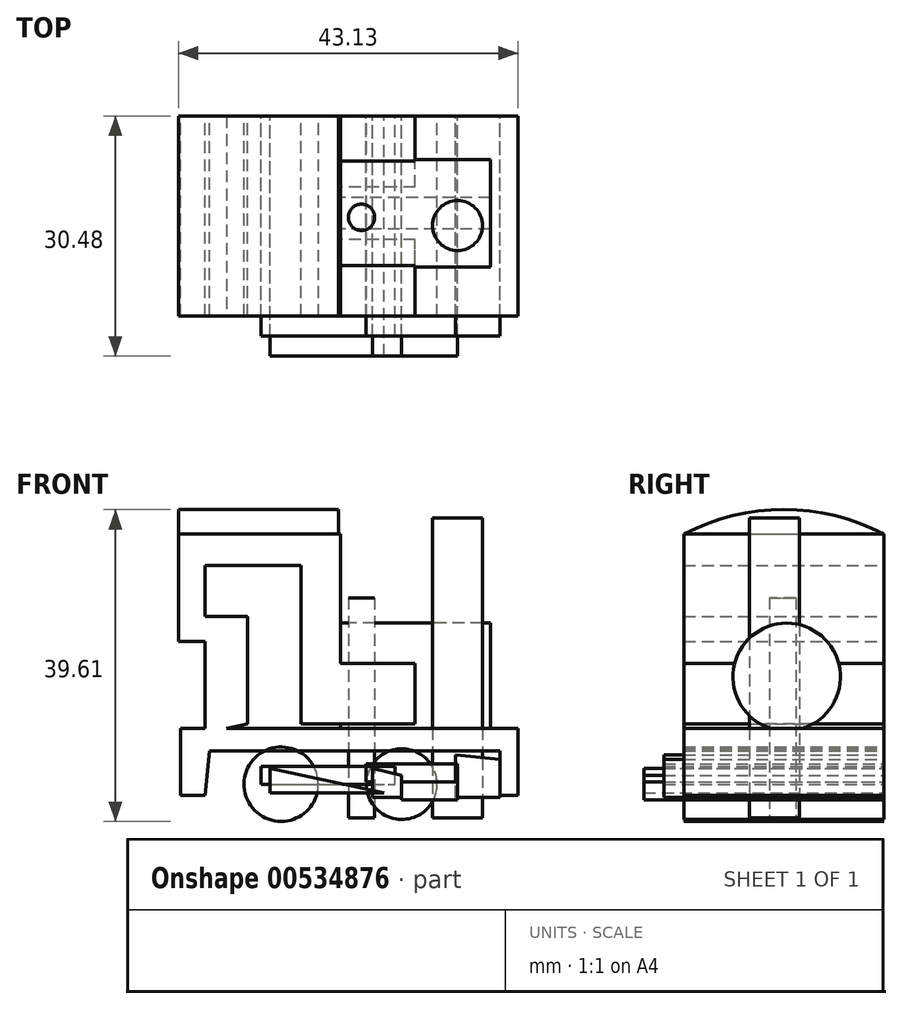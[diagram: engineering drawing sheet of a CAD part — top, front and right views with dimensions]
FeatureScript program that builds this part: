
annotation { "Feature Type Name" : "Feature", "Feature Type Description" : "" }
export const myFeature = defineFeature(function(context is Context, id is Id, definition is map)
    precondition{}
    {
        {
            var Q0;
            Q0=qCreatedBy(makeId("Front.planeOp"),FACE);
            var sketch = newSketch(context, id + "F0", { "sketchPlane" : qUnion([Q0])});
            skCircle(sketch, "E0", {"center": v(7.8, 4.26) * mm, "radius": 4.49 * mm});
            skCircle(sketch, "E1", {"center": v(-7.52, 4.26) * mm, "radius": 4.72 * mm});
            skSolve(sketch);
        }
        {
            var Q0;
            Q0=makeQuery(id+"F0.imprint","IMPRINT",FACE,{"disambiguationData":[TD([[makeQuery(id+"F0.imprint","IMPRINT",EDGE,{"derivedFrom":sQuery(id+"F0.wireOp",EDGE,"E0")}),1.0]])]});
            var Q1;
            Q1=makeQuery(id+"F0.imprint","IMPRINT",FACE,{"disambiguationData":[TD([[makeQuery(id+"F0.imprint","IMPRINT",EDGE,{"derivedFrom":sQuery(id+"F0.wireOp",EDGE,"E1")}),1.0]])]});
            extrude(context, id + "F1", {"entities" : qUnion([Q0, Q1]), "depth" : 25.4 * mm, "offsetDistance" : 25.4 * mm});
        }
        {
            var Q0;
            Q0=qCreatedBy(makeId("Front.planeOp"),FACE);
            var sketch = newSketch(context, id + "F2", { "sketchPlane" : qUnion([Q0])});
            skLineSegment(sketch, "E2", {"start": v(-16.6, 8.51) * mm, "end": v(20.29, 8.51) * mm});
            skLineSegment(sketch, "E3", {"start": v(20.29, 8.51) * mm, "end": v(20.29, 2.84) * mm});
            skLineSegment(sketch, "E4", {"start": v(20.29, 2.84) * mm, "end": v(22.56, 2.84) * mm});
            skLineSegment(sketch, "E5", {"start": v(22.56, 2.84) * mm, "end": v(22.56, 11.35) * mm});
            skLineSegment(sketch, "E6", {"start": v(22.56, 11.35) * mm, "end": v(-20.29, 11.35) * mm});
            skLineSegment(sketch, "E7", {"start": v(-20.29, 11.35) * mm, "end": v(-20.29, 2.84) * mm});
            skLineSegment(sketch, "E8", {"start": v(-20.29, 2.84) * mm, "end": v(-17.17, 2.84) * mm});
            skLineSegment(sketch, "E9", {"start": v(-17.17, 2.84) * mm, "end": v(-16.6, 8.51) * mm});
            skSolve(sketch);
        }
        {
            var Q0;
            Q0=makeQuery(id+"F2.imprint","IMPRINT",FACE,{"disambiguationData":[TD([[makeQuery(id+"F2.imprint","IMPRINT",EDGE,{"derivedFrom":sQuery(id+"F2.wireOp",EDGE,"E2")}),1.0]])]});
            extrude(context, id + "F3", {"entities" : qUnion([Q0]), "depth" : 25.4 * mm, "offsetDistance" : 25.4 * mm});
        }
        {
            var Q0;
            Q0=qCreatedBy(makeId("Front.planeOp"),FACE);
            var sketch = newSketch(context, id + "F4", { "sketchPlane" : qUnion([Q0])});
            skLineSegment(sketch, "E10", {"start": v(-17.17, 10.78) * mm, "end": v(-17.17, 22.41) * mm});
            skLineSegment(sketch, "E11", {"start": v(-17.17, 22.41) * mm, "end": v(-20.57, 22.41) * mm});
            skLineSegment(sketch, "E12", {"start": v(-20.57, 22.41) * mm, "end": v(-20.57, 36.03) * mm});
            skLineSegment(sketch, "E13", {"start": v(-20.57, 36.03) * mm, "end": v(0, 36.03) * mm});
            skLineSegment(sketch, "E14", {"start": v(0, 36.03) * mm, "end": v(0, 19.58) * mm});
            skLineSegment(sketch, "E15", {"start": v(0, 19.58) * mm, "end": v(9.5, 19.58) * mm});
            skLineSegment(sketch, "E16", {"start": v(9.5, 19.58) * mm, "end": v(9.5, 11.92) * mm});
            skLineSegment(sketch, "E17", {"start": v(9.5, 11.92) * mm, "end": v(-4.97, 11.92) * mm});
            skLineSegment(sketch, "E18", {"start": v(-4.97, 11.92) * mm, "end": v(-4.97, 32.06) * mm});
            skLineSegment(sketch, "E19", {"start": v(-4.97, 32.06) * mm, "end": v(-17.17, 32.06) * mm});
            skLineSegment(sketch, "E20", {"start": v(-17.17, 32.06) * mm, "end": v(-17.17, 25.54) * mm});
            skLineSegment(sketch, "E21", {"start": v(-17.17, 25.54) * mm, "end": v(-11.77, 25.54) * mm});
            skLineSegment(sketch, "E22", {"start": v(-11.77, 25.54) * mm, "end": v(-11.77, 11.92) * mm});
            skLineSegment(sketch, "E23", {"start": v(-11.77, 11.92) * mm, "end": v(-17.17, 10.78) * mm});
            skSolve(sketch);
        }
        {
            var Q0;
            Q0=makeQuery(id+"F4.imprint","IMPRINT",FACE,{"disambiguationData":[TD([[makeQuery(id+"F4.imprint","IMPRINT",EDGE,{"derivedFrom":sQuery(id+"F4.wireOp",EDGE,"E10")}),-1.0]])]});
            extrude(context, id + "F5", {"entities" : qUnion([Q0]), "operationType" : NewBodyOperationType.ADD, "depth" : 25.4 * mm, "offsetDistance" : 25.4 * mm});
        }
        {
            var Q0;
            Q0=qCreatedBy(makeId("Right.planeOp"),FACE);
            var sketch = newSketch(context, id + "F6", { "sketchPlane" : qUnion([Q0])});
            skCircle(sketch, "E24", {"center": v(-12.34, 17.87) * mm, "radius": 6.83 * mm});
            skSolve(sketch);
        }
        {
            var Q0;
            Q0=makeQuery(id+"F6.imprint","IMPRINT",FACE,{"disambiguationData":[TD([[makeQuery(id+"F6.imprint","IMPRINT",EDGE,{"derivedFrom":sQuery(id+"F6.wireOp",EDGE,"E24")}),1.0]])]});
            extrude(context, id + "F7", {"entities" : qUnion([Q0]), "operationType" : NewBodyOperationType.ADD, "depth" : 19.05 * mm, "offsetDistance" : 25.4 * mm});
        }
        {
            var Q0;
            Q0=qCreatedBy(makeId("Top.planeOp"),FACE);
            var sketch = newSketch(context, id + "F8", { "sketchPlane" : qUnion([Q0])});
            skCircle(sketch, "E25", {"center": v(14.9, -13.9) * mm, "radius": 3.17 * mm});
            skSolve(sketch);
        }
        {
            var Q0;
            Q0=makeQuery(id+"F8.imprint","IMPRINT",FACE,{"disambiguationData":[TD([[makeQuery(id+"F8.imprint","IMPRINT",EDGE,{"derivedFrom":sQuery(id+"F8.wireOp",EDGE,"E25")}),1.0]])]});
            extrude(context, id + "F9", {"entities" : qUnion([Q0]), "depth" : 38.1 * mm, "offsetDistance" : 25.4 * mm});
        }
        {
            var Q0;
            Q0=qCreatedBy(makeId("Front.planeOp"),FACE);
            var sketch = newSketch(context, id + "F10", { "sketchPlane" : qUnion([Q0])});
            skLineSegment(sketch, "E26", {"start": v(20.29, 7.38) * mm, "end": v(20.29, 2.55) * mm});
            skLineSegment(sketch, "E27", {"start": v(20.29, 2.55) * mm, "end": v(14.61, 2.55) * mm});
            skLineSegment(sketch, "E28", {"start": v(14.61, 2.55) * mm, "end": v(14.61, 7.94) * mm});
            skLineSegment(sketch, "E29", {"start": v(14.61, 7.94) * mm, "end": v(20.29, 7.38) * mm});
            skSolve(sketch);
        }
        {
            var Q0;
            Q0=makeQuery(id+"F10.imprint","IMPRINT",FACE,{"disambiguationData":[TD([[makeQuery(id+"F10.imprint","IMPRINT",EDGE,{"derivedFrom":sQuery(id+"F10.wireOp",EDGE,"E26")}),-1.0]])]});
            extrude(context, id + "F11", {"entities" : qUnion([Q0]), "depth" : 27.94 * mm, "offsetDistance" : 25.4 * mm});
        }
        {
            var Q0;
            Q0=qCreatedBy(makeId("Front.planeOp"),FACE);
            var sketch = newSketch(context, id + "F12", { "sketchPlane" : qUnion([Q0])});
            skLineSegment(sketch, "E30", {"start": v(-10.07, 6.53) * mm, "end": v(-10.07, 4.26) * mm});
            skLineSegment(sketch, "E31", {"start": v(-10.07, 4.26) * mm, "end": v(6.95, 4.26) * mm});
            skLineSegment(sketch, "E32", {"start": v(6.95, 4.26) * mm, "end": v(6.95, 6.53) * mm});
            skLineSegment(sketch, "E33", {"start": v(6.95, 6.53) * mm, "end": v(-10.07, 6.53) * mm});
            skSolve(sketch);
        }
        {
            var Q0;
            Q0=makeQuery(id+"F12.imprint","IMPRINT",FACE,{"disambiguationData":[TD([[makeQuery(id+"F12.imprint","IMPRINT",EDGE,{"derivedFrom":sQuery(id+"F12.wireOp",EDGE,"E30")}),1.0]])]});
            extrude(context, id + "F13", {"entities" : qUnion([Q0]), "depth" : 27.94 * mm, "offsetDistance" : 25.4 * mm});
        }
        {
            var Q0;
            Q0=qCreatedBy(makeId("Front.planeOp"),FACE);
            var sketch = newSketch(context, id + "F14", { "sketchPlane" : qUnion([Q0])});
            skLineSegment(sketch, "E34", {"start": v(14.9, 6.8) * mm, "end": v(3.26, 6.8) * mm});
            skLineSegment(sketch, "E35", {"start": v(3.26, 6.8) * mm, "end": v(3.26, 4.54) * mm});
            skLineSegment(sketch, "E36", {"start": v(3.26, 4.54) * mm, "end": v(12.06, 4.54) * mm});
            skLineSegment(sketch, "E37", {"start": v(12.06, 4.54) * mm, "end": v(14.9, 4.54) * mm});
            skLineSegment(sketch, "E38", {"start": v(14.9, 4.54) * mm, "end": v(14.9, 6.8) * mm});
            skSolve(sketch);
        }
        {
            var Q0;
            Q0=makeQuery(id+"F14.imprint","IMPRINT",FACE,{"disambiguationData":[TD([[makeQuery(id+"F14.imprint","IMPRINT",EDGE,{"derivedFrom":sQuery(id+"F14.wireOp",EDGE,"E34")}),1.0]])]});
            extrude(context, id + "F15", {"entities" : qUnion([Q0]), "depth" : 27.94 * mm, "offsetDistance" : 25.4 * mm});
        }
        {
            var Q0;
            Q0=qCreatedBy(makeId("Front.planeOp"),FACE);
            var sketch = newSketch(context, id + "F16", { "sketchPlane" : qUnion([Q0])});
            skLineSegment(sketch, "E39", {"start": v(4.11, 6.24) * mm, "end": v(4.11, 2.55) * mm});
            skLineSegment(sketch, "E40", {"start": v(4.11, 2.55) * mm, "end": v(7.8, 2.55) * mm});
            skLineSegment(sketch, "E41", {"start": v(7.8, 2.55) * mm, "end": v(7.8, 5.4) * mm});
            skLineSegment(sketch, "E42", {"start": v(7.8, 5.4) * mm, "end": v(4.11, 6.24) * mm});
            skSolve(sketch);
        }
        {
            var Q0;
            Q0=makeQuery(id+"F16.imprint","IMPRINT",FACE,{"disambiguationData":[TD([[makeQuery(id+"F16.imprint","IMPRINT",EDGE,{"derivedFrom":sQuery(id+"F16.wireOp",EDGE,"E39")}),1.0]])]});
            extrude(context, id + "F17", {"entities" : qUnion([Q0]), "depth" : 30.48 * mm, "offsetDistance" : 25.4 * mm});
        }
        {
            var Q0;
            Q0=qCreatedBy(makeId("Front.planeOp"),FACE);
            var sketch = newSketch(context, id + "F18", { "sketchPlane" : qUnion([Q0])});
            skLineSegment(sketch, "E43", {"start": v(7.8, 2.27) * mm, "end": v(14.9, 2.27) * mm});
            skLineSegment(sketch, "E44", {"start": v(14.9, 2.27) * mm, "end": v(14.9, 4.54) * mm});
            skLineSegment(sketch, "E45", {"start": v(14.9, 4.54) * mm, "end": v(7.8, 4.54) * mm});
            skLineSegment(sketch, "E46", {"start": v(7.8, 2.27) * mm, "end": v(7.8, 4.54) * mm});
            skSolve(sketch);
        }
        {
            var Q0;
            Q0=makeQuery(id+"F18.imprint","IMPRINT",FACE,{"disambiguationData":[TD([[makeQuery(id+"F18.imprint","IMPRINT",EDGE,{"derivedFrom":sQuery(id+"F18.wireOp",EDGE,"E43")}),1.0]])]});
            extrude(context, id + "F19", {"entities" : qUnion([Q0]), "depth" : 30.48 * mm, "offsetDistance" : 25.4 * mm});
        }
        {
            var Q0;
            Q0=qCreatedBy(makeId("Front.planeOp"),FACE);
            var sketch = newSketch(context, id + "F20", { "sketchPlane" : qUnion([Q0])});
            skLineSegment(sketch, "E47", {"start": v(-8.94, 6.24) * mm, "end": v(5.53, 3.12) * mm});
            skLineSegment(sketch, "E48", {"start": v(5.53, 3.12) * mm, "end": v(-8.94, 3.12) * mm});
            skLineSegment(sketch, "E49", {"start": v(-8.94, 3.12) * mm, "end": v(-8.94, 6.24) * mm});
            skSolve(sketch);
        }
        {
            var Q0;
            Q0=makeQuery(id+"F20.imprint","IMPRINT",FACE,{"disambiguationData":[TD([[makeQuery(id+"F20.imprint","IMPRINT",EDGE,{"derivedFrom":sQuery(id+"F20.wireOp",EDGE,"E47")}),-1.0]])]});
            extrude(context, id + "F21", {"entities" : qUnion([Q0]), "depth" : 30.48 * mm, "offsetDistance" : 25.4 * mm});
        }
        {
            var Q0;
            Q0=qCreatedBy(makeId("Top.planeOp"),FACE);
            var sketch = newSketch(context, id + "F22", { "sketchPlane" : qUnion([Q0])});
            skCircle(sketch, "E50", {"center": v(2.69, -12.86) * mm, "radius": 1.68 * mm});
            skSolve(sketch);
        }
        {
            var Q0;
            Q0=makeQuery(id+"F22.imprint","IMPRINT",FACE,{"disambiguationData":[TD([[makeQuery(id+"F22.imprint","IMPRINT",EDGE,{"derivedFrom":sQuery(id+"F22.wireOp",EDGE,"E50")}),1.0]])]});
            extrude(context, id + "F23", {"entities" : qUnion([Q0]), "depth" : 27.94 * mm, "offsetDistance" : 25.4 * mm});
        }
        {
            var Q0;
            Q0=makeQuery(id+"F5.opExtrude","SWEPT_FACE",FACE,{"disambiguationData":[OSD([sQuery(id+"F4.wireOp",EDGE,"E12")])]});
            var sketch = newSketch(context, id + "F24", { "sketchPlane" : qUnion([Q0])});
            skArc(sketch, "E51", {"start": v(25.4, 36.03) * mm, "mid": v(12.7, 39.14) * mm, "end": v(0, 36.03) * mm});
            skLineSegment(sketch, "E52", {"start": v(0, 36.03) * mm, "end": v(25.4, 36.03) * mm});
            skSolve(sketch);
        }
        {
            var Q0;
            Q0=makeQuery(id+"F24.imprint","IMPRINT",FACE,{"disambiguationData":[TD([[makeQuery(id+"F24.imprint","IMPRINT",EDGE,{"derivedFrom":sQuery(id+"F24.wireOp",EDGE,"E51")}),1.0]])]});
            extrude(context, id + "F25", {"entities" : qUnion([Q0]), "operationType" : NewBodyOperationType.ADD, "oppositeDirection" : true, "depth" : 20.32 * mm, "offsetDistance" : 25.4 * mm});
        }
    });
